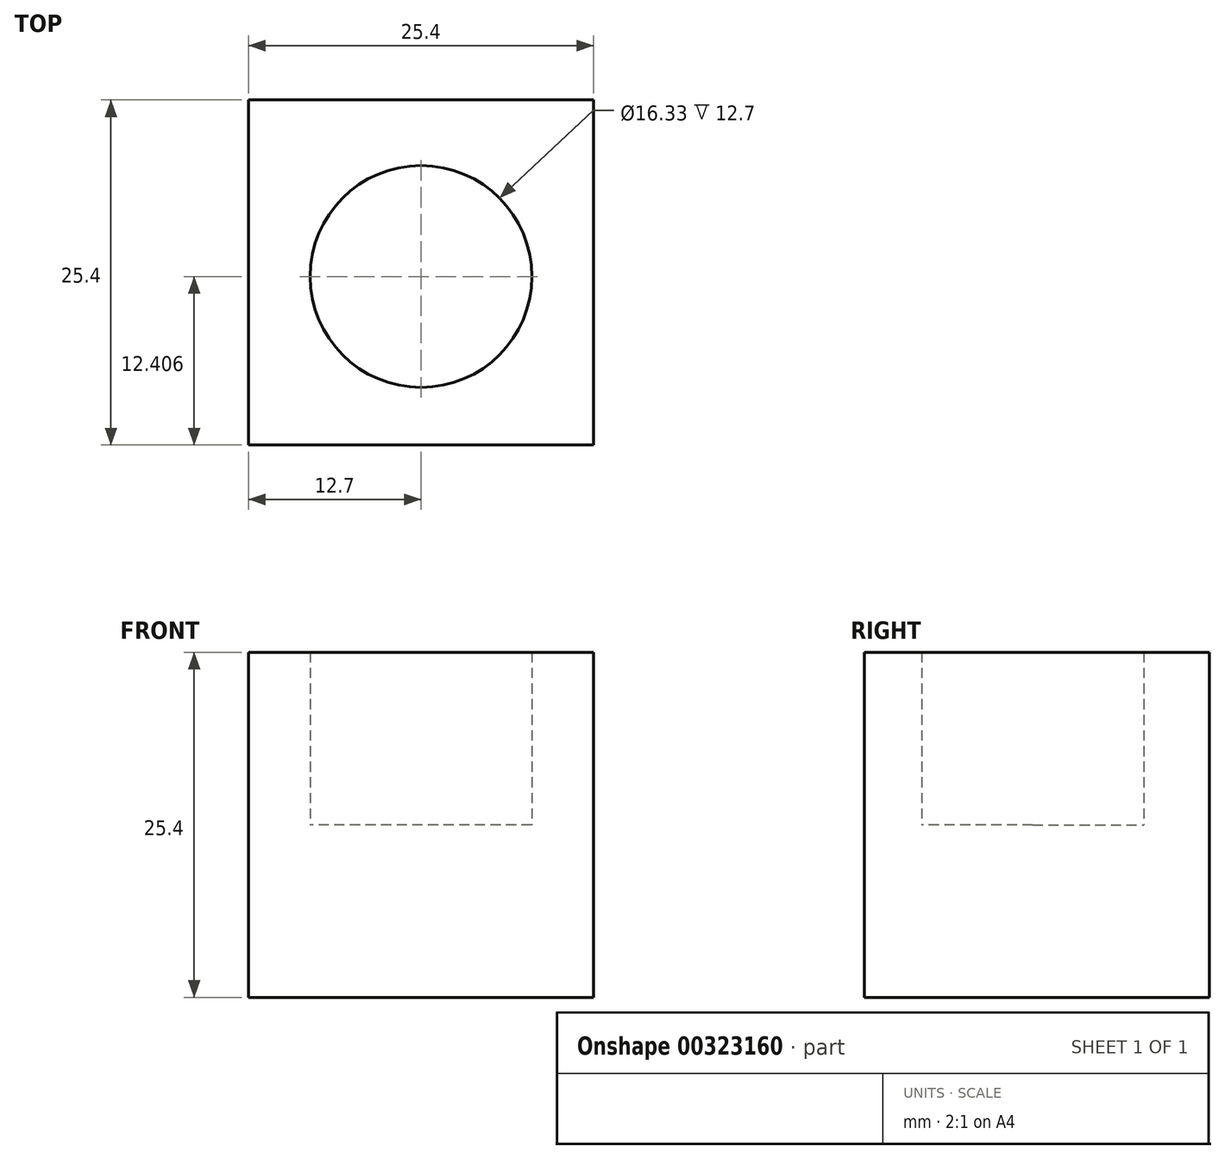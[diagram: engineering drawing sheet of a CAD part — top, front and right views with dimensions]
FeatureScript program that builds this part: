
annotation { "Feature Type Name" : "Feature", "Feature Type Description" : "" }
export const myFeature = defineFeature(function(context is Context, id is Id, definition is map)
    precondition{}
    {
        {
            var Q0;
            Q0=qCreatedBy(makeId("Front.planeOp"),FACE);
            var sketch = newSketch(context, id + "F0", { "sketchPlane" : qUnion([Q0])});
            skLineSegment(sketch, "E0.bottom", {"start": v(12.7, 12.7) * mm, "end": v(-12.7, 12.7) * mm});
            skLineSegment(sketch, "E0.top", {"start": v(12.7, -12.7) * mm, "end": v(-12.7, -12.7) * mm});
            skLineSegment(sketch, "E0.left", {"start": v(12.7, 12.7) * mm, "end": v(12.7, -12.7) * mm});
            skLineSegment(sketch, "E0.right", {"start": v(-12.7, 12.7) * mm, "end": v(-12.7, -12.7) * mm});
            skPoint(sketch, "E0.middle", {"position": v(0, 0) * mm});
            skSolve(sketch);
        }
        {
            var Q0;
            Q0 = qSketchRegion(id + "F0", true);
            extrude(context, id + "F1", {"entities" : qUnion([Q0]), "depth" : 25.4 * mm});
        }
        {
            var Q0;
            Q0=qCreatedBy(makeId("Top.planeOp"),FACE);
            var sketch = newSketch(context, id + "F2", { "sketchPlane" : qUnion([Q0])});
            skCircle(sketch, "E1", {"center": v(0, -13) * mm, "radius": 8.16 * mm});
            skSolve(sketch);
        }
        {
            var Q0;
            Q0 = qSketchRegion(id + "F2", true);
            extrude(context, id + "F3", {"entities" : qUnion([Q0]), "operationType" : NewBodyOperationType.REMOVE, "endBound" : BoundingType.THROUGH_ALL, "depth" : 25.4 * mm});
        }
    });
